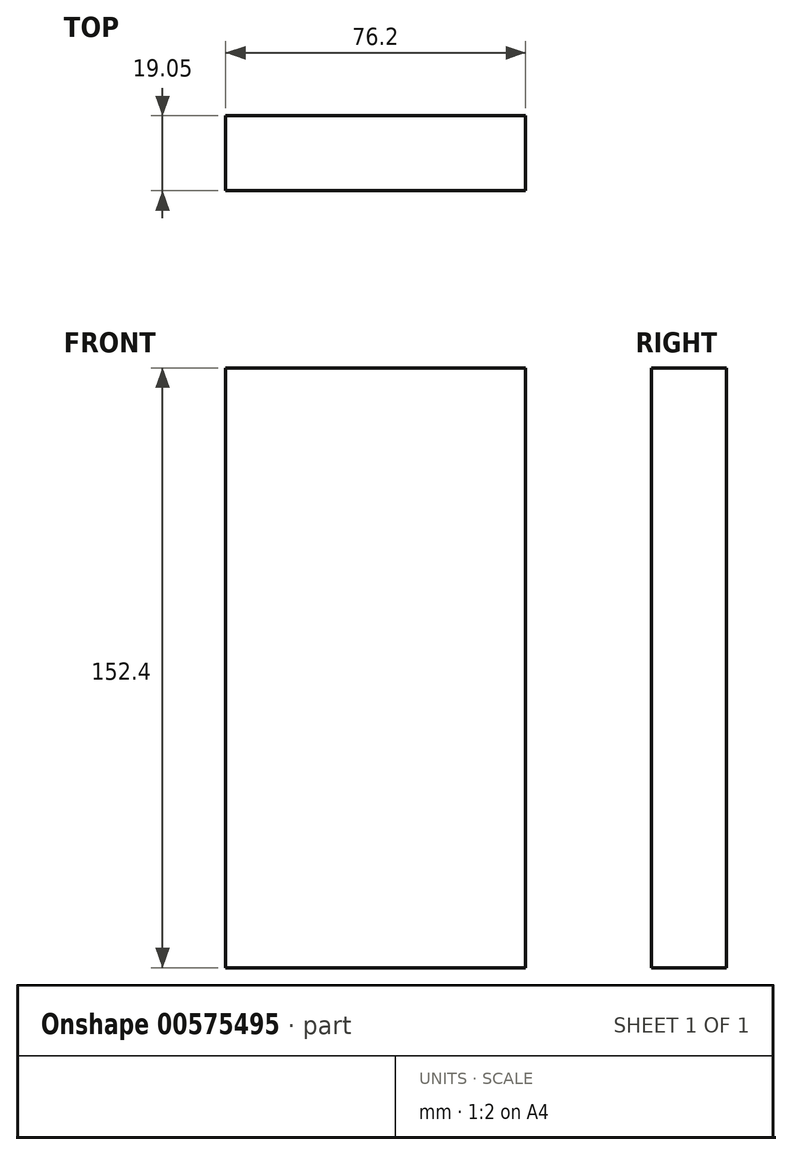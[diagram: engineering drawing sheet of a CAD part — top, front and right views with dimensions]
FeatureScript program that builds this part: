
annotation { "Feature Type Name" : "Feature", "Feature Type Description" : "" }
export const myFeature = defineFeature(function(context is Context, id is Id, definition is map)
    precondition{}
    {
        {
            var Q0;
            Q0=qCreatedBy(makeId("Front.planeOp"),FACE);
            var sketch = newSketch(context, id + "F0", { "sketchPlane" : qUnion([Q0])});
            skLineSegment(sketch, "E0.bottom", {"start": v(-76.2, 116.21) * mm, "end": v(0, 116.21) * mm});
            skLineSegment(sketch, "E0.top", {"start": v(-76.2, -36.19) * mm, "end": v(0, -36.19) * mm});
            skLineSegment(sketch, "E0.left", {"start": v(-76.2, 116.21) * mm, "end": v(-76.2, -36.19) * mm});
            skLineSegment(sketch, "E0.right", {"start": v(0, 116.21) * mm, "end": v(0, -36.19) * mm});
            skLineSegment(sketch, "E1", {"start": v(-76.2, 116.21) * mm, "end": v(-38.1, 116.21) * mm});
            skSolve(sketch);
        }
        {
            var Q0;
            Q0 = qSketchRegion(id + "F0", true);
            extrude(context, id + "F1", {"entities" : qUnion([Q0]), "depth" : 19.05 * mm, "offsetDistance" : 25.4 * mm});
        }
    });
